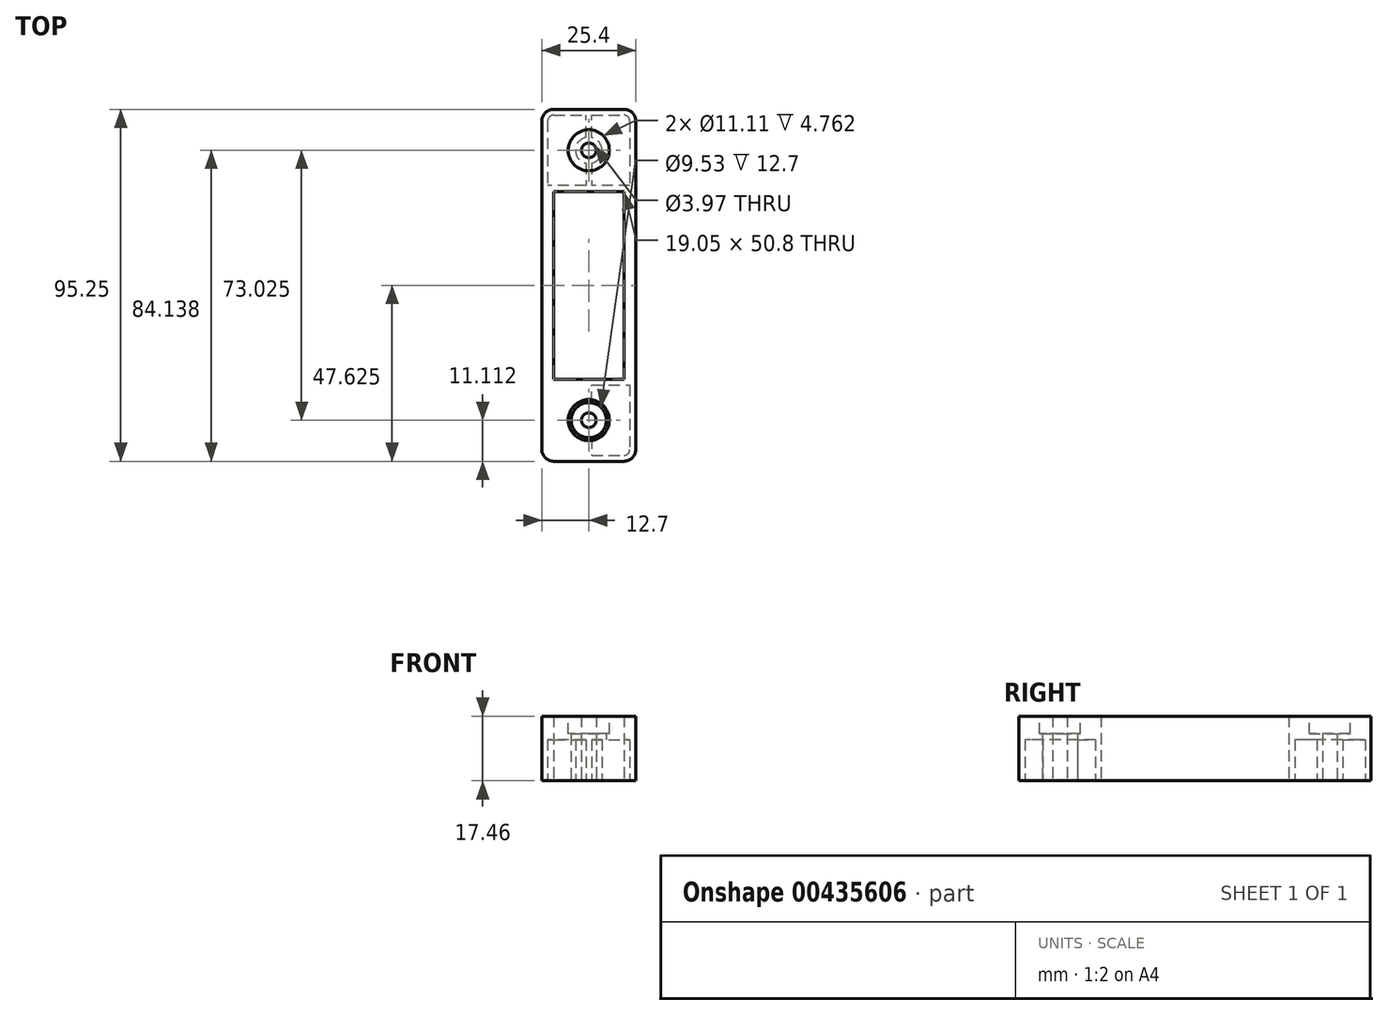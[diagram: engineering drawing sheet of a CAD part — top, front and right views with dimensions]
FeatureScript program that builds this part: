
annotation { "Feature Type Name" : "Feature", "Feature Type Description" : "" }
export const myFeature = defineFeature(function(context is Context, id is Id, definition is map)
    precondition{}
    {
        {
            var Q0;
            Q0=qCreatedBy(makeId("Top.planeOp"),FACE);
            var sketch = newSketch(context, id + "F0", { "sketchPlane" : qUnion([Q0])});
            skLineSegment(sketch, "E0.bottom", {"start": v(3.18, 0) * mm, "end": v(22.23, 0) * mm});
            skLineSegment(sketch, "E0.top", {"start": v(3.18, -95.25) * mm, "end": v(22.23, -95.25) * mm});
            skLineSegment(sketch, "E0.left", {"start": v(0, -3.17) * mm, "end": v(0, -92.08) * mm});
            skLineSegment(sketch, "E0.right", {"start": v(25.4, -3.17) * mm, "end": v(25.4, -92.08) * mm});
            skPoint(sketch, "E1.visualSharp", {"position": v(0, 0) * mm});
            skArc(sketch, "E1.filletArc", {"start": v(3.18, 0) * mm, "mid": v(0.93, -0.93) * mm, "end": v(0, -3.18) * mm});
            skPoint(sketch, "E2.visualSharp", {"position": v(0, -95.25) * mm});
            skArc(sketch, "E2.filletArc", {"start": v(0, -92.08) * mm, "mid": v(0.93, -94.32) * mm, "end": v(3.18, -95.25) * mm});
            skPoint(sketch, "E3.visualSharp", {"position": v(25.4, -95.25) * mm});
            skArc(sketch, "E3.filletArc", {"start": v(22.23, -95.25) * mm, "mid": v(24.47, -94.32) * mm, "end": v(25.4, -92.08) * mm});
            skPoint(sketch, "E4.visualSharp", {"position": v(25.4, 0) * mm});
            skArc(sketch, "E4.filletArc", {"start": v(25.4, -3.17) * mm, "mid": v(24.47, -0.93) * mm, "end": v(22.23, 0) * mm});
            skLineSegment(sketch, "E5", {"start": v(0, -47.63) * mm, "end": v(25.4, -47.62) * mm, "construction": true});
            skPoint(sketch, "E6", {"position": v(12.7, -47.62) * mm});
            skLineSegment(sketch, "E7", {"start": v(12.7, 0) * mm, "end": v(12.7, -95.25) * mm, "construction": true});
            skLineSegment(sketch, "E8", {"start": v(12.7, -22.23) * mm, "end": v(22.23, -22.23) * mm});
            skLineSegment(sketch, "E9", {"start": v(22.23, -22.23) * mm, "end": v(22.23, -47.62) * mm});
            skLineSegment(sketch, "E10.MirrorCS", {"start": v(22.23, -73.02) * mm, "end": v(22.23, -47.62) * mm});
            skLineSegment(sketch, "E11.MirrorCS", {"start": v(12.7, -73.02) * mm, "end": v(22.23, -73.02) * mm});
            skLineSegment(sketch, "E12.MirrorCS", {"start": v(12.7, -22.23) * mm, "end": v(3.18, -22.23) * mm});
            skLineSegment(sketch, "E13.MirrorCS", {"start": v(3.18, -22.22) * mm, "end": v(3.18, -47.62) * mm});
            skLineSegment(sketch, "E14.MirrorCS", {"start": v(3.17, -73.02) * mm, "end": v(3.18, -47.62) * mm});
            skLineSegment(sketch, "E15.MirrorCS", {"start": v(12.7, -73.02) * mm, "end": v(3.17, -73.02) * mm});
            skPoint(sketch, "E16.center.orphan", {"position": v(12.7, -11.11) * mm});
            skSolve(sketch);
        }
        {
            var Q0;
            Q0=makeQuery(id+"F0.imprint","IMPRINT",FACE,{"disambiguationData":[TD([[makeQuery(id+"F0.imprint","IMPRINT",EDGE,{"derivedFrom":sQuery(id+"F0.wireOp",EDGE,"E0.bottom")}),-1.0]])]});
            extrude(context, id + "F1", {"entities" : qUnion([Q0]), "depth" : 17.46 * mm});
        }
        {
            var Q0;
            Q0=makeQuery(id+"F1.opExtrude","CAP_FACE",FACE,{"disambiguationData":[OSD([sQuery(id+"F0.wireOp",EDGE,"E0.bottom"),sQuery(id+"F0.wireOp",EDGE,"E0.top"),sQuery(id+"F0.wireOp",EDGE,"E0.left"),sQuery(id+"F0.wireOp",EDGE,"E0.right"),sQuery(id+"F0.wireOp",EDGE,"E1.filletArc"),sQuery(id+"F0.wireOp",EDGE,"E2.filletArc"),sQuery(id+"F0.wireOp",EDGE,"E3.filletArc"),sQuery(id+"F0.wireOp",EDGE,"E4.filletArc")])],"isStart":false});
            var sketch = newSketch(context, id + "F2", { "sketchPlane" : qUnion([Q0])});
            skPoint(sketch, "E17.visualSharp", {"position": v(31.75, 0) * mm});
            skLineSegment(sketch, "E18", {"start": v(0, -47.62) * mm, "end": v(25.4, -47.62) * mm, "construction": true});
            skLineSegment(sketch, "E19", {"start": v(2.38, -22.22) * mm, "end": v(2.38, -47.62) * mm});
            skLineSegment(sketch, "E20", {"start": v(2.38, -22.22) * mm, "end": v(0, -22.22) * mm});
            skLineSegment(sketch, "E21", {"start": v(0, -22.22) * mm, "end": v(0, -47.62) * mm});
            skLineSegment(sketch, "E22.MirrorCS", {"start": v(2.38, -73.02) * mm, "end": v(0, -73.02) * mm});
            skLineSegment(sketch, "E23.MirrorCS", {"start": v(2.38, -73.02) * mm, "end": v(2.38, -47.62) * mm});
            skLineSegment(sketch, "E24.MirrorCS", {"start": v(0, -73.02) * mm, "end": v(0, -47.62) * mm});
            skLineSegment(sketch, "E25", {"start": v(12.7, 0) * mm, "end": v(12.7, -95.25) * mm, "construction": true});
            skLineSegment(sketch, "E26.MirrorCS", {"start": v(23.02, -22.22) * mm, "end": v(25.4, -22.22) * mm});
            skLineSegment(sketch, "E27.MirrorCS", {"start": v(23.02, -22.22) * mm, "end": v(23.02, -47.62) * mm});
            skLineSegment(sketch, "E28.MirrorCS", {"start": v(23.02, -73.02) * mm, "end": v(23.02, -47.62) * mm});
            skLineSegment(sketch, "E29.MirrorCS", {"start": v(23.02, -73.02) * mm, "end": v(25.4, -73.02) * mm});
            skLineSegment(sketch, "E30.MirrorCS", {"start": v(25.4, -73.02) * mm, "end": v(25.4, -47.62) * mm});
            skLineSegment(sketch, "E31.MirrorCS", {"start": v(25.4, -22.22) * mm, "end": v(25.4, -47.62) * mm});
            skSolve(sketch);
        }
        {
            var Q0;
            Q0=makeQuery(id+"F1.opExtrude","CAP_FACE",FACE,{"disambiguationData":[OSD([sQuery(id+"F0.wireOp",EDGE,"E0.bottom"),sQuery(id+"F0.wireOp",EDGE,"E0.top"),sQuery(id+"F0.wireOp",EDGE,"E0.left"),sQuery(id+"F0.wireOp",EDGE,"E0.right"),sQuery(id+"F0.wireOp",EDGE,"E1.filletArc"),sQuery(id+"F0.wireOp",EDGE,"E2.filletArc"),sQuery(id+"F0.wireOp",EDGE,"E3.filletArc"),sQuery(id+"F0.wireOp",EDGE,"E4.filletArc")])],"isStart":true});
            var sketch = newSketch(context, id + "F3", { "sketchPlane" : qUnion([Q0])});
            skLineSegment(sketch, "E32", {"start": v(12.7, 0) * mm, "end": v(12.7, 95.25) * mm, "construction": true});
            skCircle(sketch, "E33", {"center": v(12.7, 11.11) * mm, "radius": 1.98 * mm});
            skLineSegment(sketch, "E34", {"start": v(0, 47.62) * mm, "end": v(25.4, 47.62) * mm, "construction": true});
            skCircle(sketch, "E35.MirrorC", {"center": v(12.7, 84.14) * mm, "radius": 1.98 * mm});
            skCircle(sketch, "E36", {"center": v(12.7, 84.14) * mm, "radius": 4.76 * mm});
            skCircle(sketch, "E37.MirrorC", {"center": v(12.7, 11.11) * mm, "radius": 4.76 * mm});
            skSolve(sketch);
        }
        {
            var Q0;
            Q0=makeQuery(id+"F3.imprint","IMPRINT",FACE,{"disambiguationData":[TD([[makeQuery(id+"F3.imprint","IMPRINT",EDGE,{"derivedFrom":sQuery(id+"F3.wireOp",EDGE,"E33")}),1.0]])]});
            var Q1;
            Q1=makeQuery(id+"F3.imprint","IMPRINT",FACE,{"disambiguationData":[TD([[makeQuery(id+"F3.imprint","IMPRINT",EDGE,{"derivedFrom":sQuery(id+"F3.wireOp",EDGE,"E35.MirrorC")}),-1.0]])]});
            var Q2;
            Q2=sQuery(id+"F3.wireOp",EDGE,"E33");
            var Q3;
            Q3=sQuery(id+"F3.wireOp",EDGE,"E35.MirrorC");
            extrude(context, id + "F4", {"entities" : qUnion([Q0, Q1]), "operationType" : NewBodyOperationType.REMOVE, "surfaceEntities" : qUnion([Q2, Q3]), "endBound" : BoundingType.THROUGH_ALL, "oppositeDirection" : true, "depth" : 25.4 * mm});
        }
        {
            var Q0;
            Q0=makeQuery(id+"F0.imprint","IMPRINT",FACE,{"disambiguationData":[TD([[makeQuery(id+"F0.imprint","IMPRINT",EDGE,{"derivedFrom":sQuery(id+"F0.wireOp",EDGE,"E8")}),-1.0]])]});
            extrude(context, id + "F5", {"entities" : qUnion([Q0]), "operationType" : NewBodyOperationType.REMOVE, "depth" : 3.17 * mm});
        }
        {
            var Q0;
            Q0=makeQuery(id+"F1.opExtrude","CAP_FACE",FACE,{"disambiguationData":[OSD([sQuery(id+"F0.wireOp",EDGE,"E0.bottom"),sQuery(id+"F0.wireOp",EDGE,"E0.top"),sQuery(id+"F0.wireOp",EDGE,"E0.left"),sQuery(id+"F0.wireOp",EDGE,"E0.right"),sQuery(id+"F0.wireOp",EDGE,"E1.filletArc"),sQuery(id+"F0.wireOp",EDGE,"E2.filletArc"),sQuery(id+"F0.wireOp",EDGE,"E3.filletArc"),sQuery(id+"F0.wireOp",EDGE,"E4.filletArc"),sQuery(id+"F0.wireOp",EDGE,"E8"),sQuery(id+"F0.wireOp",EDGE,"E9"),sQuery(id+"F0.wireOp",EDGE,"E10.MirrorCS"),sQuery(id+"F0.wireOp",EDGE,"E11.MirrorCS"),sQuery(id+"F0.wireOp",EDGE,"E12.MirrorCS"),sQuery(id+"F0.wireOp",EDGE,"E13.MirrorCS"),sQuery(id+"F0.wireOp",EDGE,"E14.MirrorCS"),sQuery(id+"F0.wireOp",EDGE,"E15.MirrorCS")])],"isStart":true});
            var sketch = newSketch(context, id + "F6", { "sketchPlane" : qUnion([Q0])});
            skLineSegment(sketch, "E38", {"start": v(0, 39.8) * mm, "end": v(0, 49.47) * mm, "construction": true});
            skLineSegment(sketch, "E39", {"start": v(0, 47.62) * mm, "end": v(25.4, 47.62) * mm, "construction": true});
            skArc(sketch, "E40", {"start": v(11.9, 87.62) * mm, "mid": v(9.13, 84.14) * mm, "end": v(11.9, 80.65) * mm});
            skLineSegment(sketch, "E41", {"start": v(12.7, 47.62) * mm, "end": v(12.7, 95.25) * mm, "construction": true});
            skLineSegment(sketch, "E42.0", {"start": v(3.18, 93.66) * mm, "end": v(22.22, 93.66) * mm});
            skLineSegment(sketch, "E42.1", {"start": v(1.59, 3.18) * mm, "end": v(1.59, 92.08) * mm});
            skLineSegment(sketch, "E42.2", {"start": v(3.18, 1.59) * mm, "end": v(22.22, 1.59) * mm});
            skLineSegment(sketch, "E42.3", {"start": v(23.81, 3.18) * mm, "end": v(23.81, 92.08) * mm});
            skPoint(sketch, "E43.visualSharp", {"position": v(23.81, 93.66) * mm});
            skArc(sketch, "E43.filletArc", {"start": v(23.81, 92.08) * mm, "mid": v(23.35, 93.2) * mm, "end": v(22.22, 93.66) * mm});
            skPoint(sketch, "E44.visualSharp", {"position": v(1.59, 93.66) * mm});
            skArc(sketch, "E44.filletArc", {"start": v(3.18, 93.66) * mm, "mid": v(2.05, 93.2) * mm, "end": v(1.59, 92.08) * mm});
            skPoint(sketch, "E45.visualSharp", {"position": v(1.59, 1.59) * mm});
            skArc(sketch, "E45.filletArc", {"start": v(1.59, 3.18) * mm, "mid": v(2.05, 2.05) * mm, "end": v(3.18, 1.59) * mm});
            skPoint(sketch, "E46.visualSharp", {"position": v(23.81, 1.59) * mm});
            skArc(sketch, "E46.filletArc", {"start": v(22.22, 1.59) * mm, "mid": v(23.35, 2.05) * mm, "end": v(23.81, 3.18) * mm});
            skLineSegment(sketch, "E47", {"start": v(11.9, 87.62) * mm, "end": v(11.9, 93.66) * mm});
            skLineSegment(sketch, "E48.MirrorCS", {"start": v(13.5, 87.62) * mm, "end": v(13.5, 93.66) * mm});
            skLineSegment(sketch, "E49", {"start": v(11.9, 80.65) * mm, "end": v(11.9, 74.61) * mm});
            skLineSegment(sketch, "E50.MirrorCS", {"start": v(13.5, 80.65) * mm, "end": v(13.5, 74.61) * mm});
            skArc(sketch, "E51.trimOffspring", {"start": v(13.5, 80.65) * mm, "mid": v(16.27, 84.14) * mm, "end": v(13.5, 87.62) * mm});
            skPoint(sketch, "E52.MirrorCS.end.orphan", {"position": v(13.5, 1.59) * mm});
            skPoint(sketch, "E52.MirrorCS.start.orphan", {"position": v(13.5, 7.63) * mm});
            skPoint(sketch, "E53.MirrorCS.end.orphan", {"position": v(11.9, 1.59) * mm});
            skPoint(sketch, "E53.MirrorCS.start.orphan", {"position": v(11.9, 7.63) * mm});
            skLineSegment(sketch, "E54.MirrorCS", {"start": v(11.9, 7.63) * mm, "end": v(11.9, 1.59) * mm});
            skLineSegment(sketch, "E55.MirrorCS", {"start": v(13.5, 7.63) * mm, "end": v(13.5, 1.59) * mm});
            skArc(sketch, "E56.MirrorCS", {"start": v(11.9, 7.63) * mm, "mid": v(9.13, 11.11) * mm, "end": v(11.9, 14.6) * mm});
            skArc(sketch, "E57.MirrorCS", {"start": v(13.5, 14.6) * mm, "mid": v(16.27, 11.11) * mm, "end": v(13.5, 7.63) * mm});
            skLineSegment(sketch, "E58.MirrorCS", {"start": v(11.9, 14.6) * mm, "end": v(11.9, 20.64) * mm});
            skLineSegment(sketch, "E59.MirrorCS", {"start": v(13.5, 14.6) * mm, "end": v(13.5, 20.64) * mm});
            skLineSegment(sketch, "E60.0", {"start": v(1.59, 74.61) * mm, "end": v(11.9, 74.61) * mm});
            skLineSegment(sketch, "E60.1", {"start": v(1.59, 74.61) * mm, "end": v(1.59, 20.64) * mm});
            skLineSegment(sketch, "E60.2", {"start": v(23.81, 20.64) * mm, "end": v(13.5, 20.64) * mm});
            skLineSegment(sketch, "E60.3", {"start": v(23.81, 20.64) * mm, "end": v(23.81, 74.61) * mm});
            skLineSegment(sketch, "E61.trimOffspring", {"start": v(13.5, 74.61) * mm, "end": v(23.81, 74.61) * mm});
            skPoint(sketch, "E62.orphan", {"position": v(13.5, 73.02) * mm});
            skPoint(sketch, "E63.orphan", {"position": v(11.9, 73.02) * mm});
            skPoint(sketch, "E64.orphan", {"position": v(11.9, 22.22) * mm});
            skLineSegment(sketch, "E65.trimOffspring", {"start": v(11.9, 20.64) * mm, "end": v(1.59, 20.64) * mm});
            skPoint(sketch, "E66.orphan", {"position": v(13.5, 22.22) * mm});
            skSolve(sketch);
        }
        {
            var Q0;
            Q0=makeQuery(id+"F6.imprint","IMPRINT",FACE,{"disambiguationData":[TD([[makeQuery(id+"F6.imprint","IMPRINT",EDGE,{"derivedFrom":makeQuery(id+"F4.boolean.opBoolean","COPY",EDGE,{"derivedFrom":makeQuery(id+"F4.opExtrude","CAP_EDGE",EDGE,{"disambiguationData":[OSD([sQuery(id+"F3.wireOp",EDGE,"E33")])],"isStart":true})})}),1.0]])]});
            var Q1;
            Q1=makeQuery(id+"F6.imprint","IMPRINT",FACE,{"disambiguationData":[TD([[makeQuery(id+"F6.imprint","IMPRINT",EDGE,{"derivedFrom":makeQuery(id+"F4.boolean.opBoolean","COPY",EDGE,{"derivedFrom":makeQuery(id+"F4.opExtrude","CAP_EDGE",EDGE,{"disambiguationData":[OSD([sQuery(id+"F3.wireOp",EDGE,"E35.MirrorC")])],"isStart":true})})}),-1.0]])]});
            var Q2;
            Q2=makeQuery(id+"F6.imprint","IMPRINT",FACE,{"disambiguationData":[TD([[makeQuery(id+"F6.imprint","IMPRINT",EDGE,{"derivedFrom":sQuery(id+"F6.wireOp",EDGE,"E42.3")}),1.0]])]});
            var Q3;
            Q3=makeQuery(id+"F6.imprint","IMPRINT",FACE,{"disambiguationData":[TD([[makeQuery(id+"F6.imprint","IMPRINT",EDGE,{"derivedFrom":sQuery(id+"F6.wireOp",EDGE,"E40")}),-1.0]])]});
            var Q4;
            {var subQ2=sQuery(id+"F6.wireOp",EDGE,"E45.filletArc");Q4=makeQuery(id+"F6.imprint","IMPRINT",FACE,{"disambiguationData":[TD([[makeQuery(id+"F6.imprint","IMPRINT",EDGE,{"derivedFrom":subQ2}),1.0]])]});}
            extrude(context, id + "F7", {"entities" : qUnion([Q0, Q1, Q2, Q3, Q4]), "operationType" : NewBodyOperationType.REMOVE, "oppositeDirection" : true, "depth" : 11.1 * mm});
        }
        {
            var Q0;
            Q0=makeQuery(id+"F1.opExtrude","CAP_FACE",FACE,{"disambiguationData":[OSD([sQuery(id+"F0.wireOp",EDGE,"E0.bottom"),sQuery(id+"F0.wireOp",EDGE,"E0.top"),sQuery(id+"F0.wireOp",EDGE,"E0.left"),sQuery(id+"F0.wireOp",EDGE,"E0.right"),sQuery(id+"F0.wireOp",EDGE,"E1.filletArc"),sQuery(id+"F0.wireOp",EDGE,"E2.filletArc"),sQuery(id+"F0.wireOp",EDGE,"E3.filletArc"),sQuery(id+"F0.wireOp",EDGE,"E4.filletArc"),sQuery(id+"F0.wireOp",EDGE,"E8"),sQuery(id+"F0.wireOp",EDGE,"E9"),sQuery(id+"F0.wireOp",EDGE,"E10.MirrorCS"),sQuery(id+"F0.wireOp",EDGE,"E11.MirrorCS"),sQuery(id+"F0.wireOp",EDGE,"E12.MirrorCS"),sQuery(id+"F0.wireOp",EDGE,"E13.MirrorCS"),sQuery(id+"F0.wireOp",EDGE,"E14.MirrorCS"),sQuery(id+"F0.wireOp",EDGE,"E15.MirrorCS")])],"isStart":false});
            var sketch = newSketch(context, id + "F8", { "sketchPlane" : qUnion([Q0])});
            skCircle(sketch, "E67", {"center": v(12.7, -11.11) * mm, "radius": 5.56 * mm});
            skCircle(sketch, "E68", {"center": v(12.7, -84.14) * mm, "radius": 5.56 * mm});
            skSolve(sketch);
        }
        {
            var Q0;
            Q0=makeQuery(id+"F8.imprint","IMPRINT",FACE,{"disambiguationData":[TD([[makeQuery(id+"F8.imprint","IMPRINT",EDGE,{"derivedFrom":makeQuery(id+"F4.boolean.opBoolean","INTERSECT",EDGE,{"derivedFrom":[makeQuery(id+"F1.opExtrude","CAP_FACE",FACE,{"disambiguationData":[OSD([sQuery(id+"F0.wireOp",EDGE,"E0.bottom"),sQuery(id+"F0.wireOp",EDGE,"E0.top"),sQuery(id+"F0.wireOp",EDGE,"E0.left"),sQuery(id+"F0.wireOp",EDGE,"E0.right"),sQuery(id+"F0.wireOp",EDGE,"E1.filletArc"),sQuery(id+"F0.wireOp",EDGE,"E2.filletArc"),sQuery(id+"F0.wireOp",EDGE,"E3.filletArc"),sQuery(id+"F0.wireOp",EDGE,"E4.filletArc"),sQuery(id+"F0.wireOp",EDGE,"E8"),sQuery(id+"F0.wireOp",EDGE,"E9"),sQuery(id+"F0.wireOp",EDGE,"E10.MirrorCS"),sQuery(id+"F0.wireOp",EDGE,"E11.MirrorCS"),sQuery(id+"F0.wireOp",EDGE,"E12.MirrorCS"),sQuery(id+"F0.wireOp",EDGE,"E13.MirrorCS"),sQuery(id+"F0.wireOp",EDGE,"E14.MirrorCS"),sQuery(id+"F0.wireOp",EDGE,"E15.MirrorCS")])],"isStart":false}),makeQuery(id+"F4.opExtrude","SWEPT_FACE",FACE,{"disambiguationData":[OSD([sQuery(id+"F3.wireOp",EDGE,"E33")])]})]})}),1.0]])]});
            var Q1;
            Q1=makeQuery(id+"F8.imprint","IMPRINT",FACE,{"disambiguationData":[TD([[makeQuery(id+"F8.imprint","IMPRINT",EDGE,{"derivedFrom":makeQuery(id+"F4.boolean.opBoolean","INTERSECT",EDGE,{"derivedFrom":[makeQuery(id+"F1.opExtrude","CAP_FACE",FACE,{"disambiguationData":[OSD([sQuery(id+"F0.wireOp",EDGE,"E0.bottom"),sQuery(id+"F0.wireOp",EDGE,"E0.top"),sQuery(id+"F0.wireOp",EDGE,"E0.left"),sQuery(id+"F0.wireOp",EDGE,"E0.right"),sQuery(id+"F0.wireOp",EDGE,"E1.filletArc"),sQuery(id+"F0.wireOp",EDGE,"E2.filletArc"),sQuery(id+"F0.wireOp",EDGE,"E3.filletArc"),sQuery(id+"F0.wireOp",EDGE,"E4.filletArc"),sQuery(id+"F0.wireOp",EDGE,"E8"),sQuery(id+"F0.wireOp",EDGE,"E9"),sQuery(id+"F0.wireOp",EDGE,"E10.MirrorCS"),sQuery(id+"F0.wireOp",EDGE,"E11.MirrorCS"),sQuery(id+"F0.wireOp",EDGE,"E12.MirrorCS"),sQuery(id+"F0.wireOp",EDGE,"E13.MirrorCS"),sQuery(id+"F0.wireOp",EDGE,"E14.MirrorCS"),sQuery(id+"F0.wireOp",EDGE,"E15.MirrorCS")])],"isStart":false}),makeQuery(id+"F4.opExtrude","SWEPT_FACE",FACE,{"disambiguationData":[OSD([sQuery(id+"F3.wireOp",EDGE,"E35.MirrorC")])]})]})}),-1.0]])]});
            var Q2;
            Q2=makeQuery(id+"F8.imprint","IMPRINT",FACE,{"disambiguationData":[TD([[makeQuery(id+"F8.imprint","IMPRINT",EDGE,{"derivedFrom":sQuery(id+"F8.wireOp",EDGE,"E68")}),1.0]])]});
            var Q3;
            Q3=makeQuery(id+"F8.imprint","IMPRINT",FACE,{"disambiguationData":[TD([[makeQuery(id+"F8.imprint","IMPRINT",EDGE,{"derivedFrom":sQuery(id+"F8.wireOp",EDGE,"E67")}),1.0]])]});
            extrude(context, id + "F9", {"entities" : qUnion([Q0, Q1, Q2, Q3]), "operationType" : NewBodyOperationType.REMOVE, "oppositeDirection" : true, "depth" : 4.76 * mm});
        }
    });
